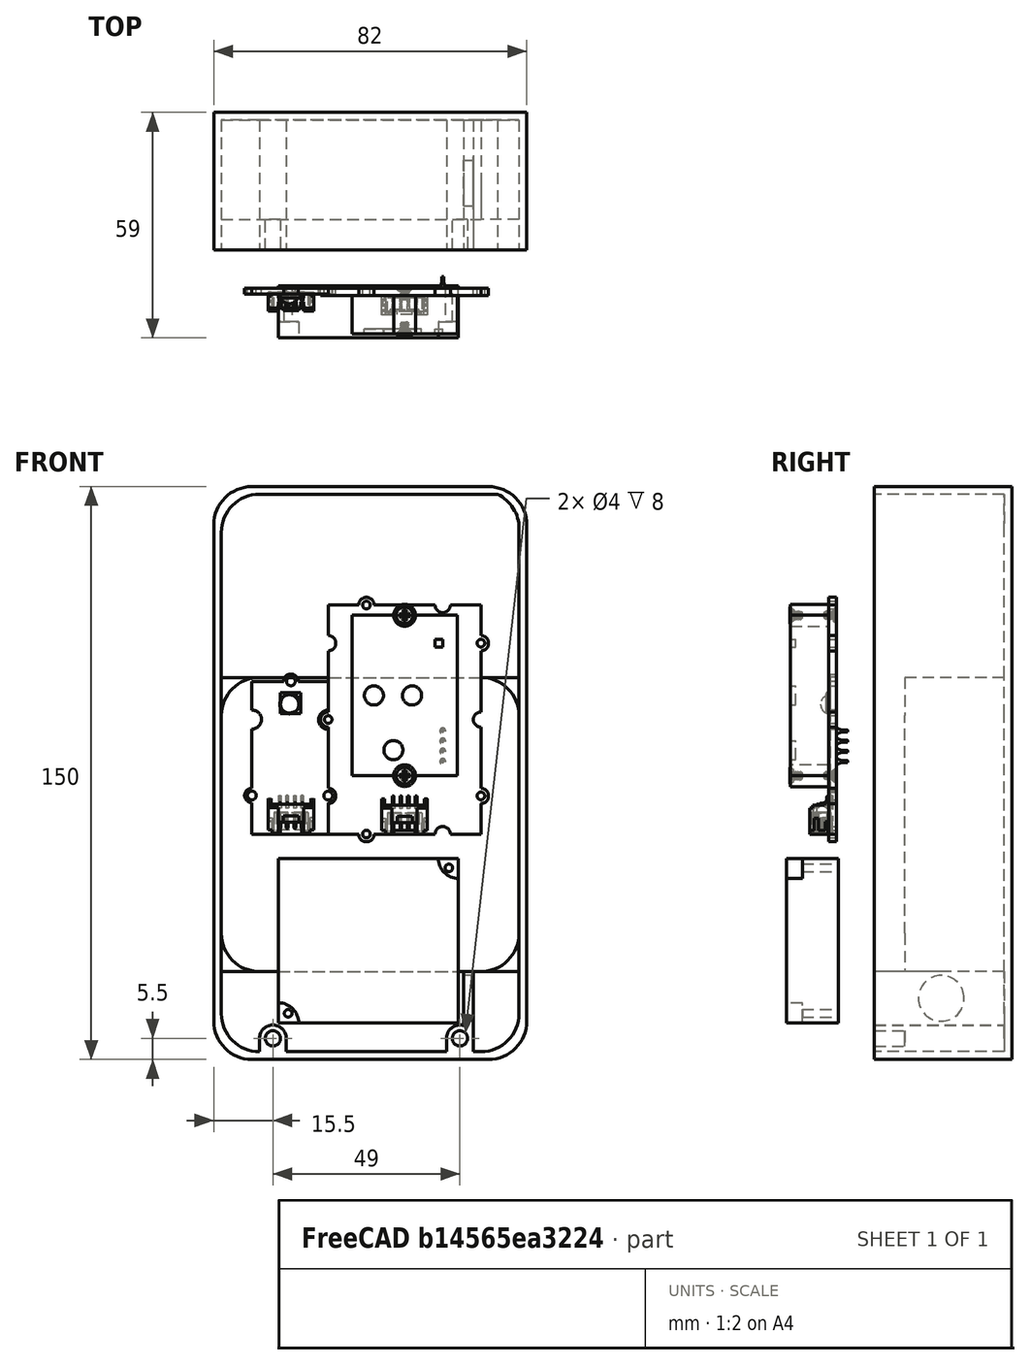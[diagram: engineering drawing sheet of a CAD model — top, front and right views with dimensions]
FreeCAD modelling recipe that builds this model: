
FCSTD DOCUMENT  (FreeCAD 0.20R29177 +233 (Git))
Label: wearableCad
License: All rights reserved
LicenseURL: http://en.wikipedia.org/wiki/All_rights_reserved
objects: Part::Cylinder×26, Part::Box×23, Part::Cut×22, Part::MultiFuse×11, Part::Feature×3
note: 85 computed .brp shape members not serialized (recipe doc carries the construction recipe); baked Part::Feature solids carry a one-line shape summary decoded from their .brp

FEATURE [Part::Feature] Feature  label="Odroid-C4"
  Placement = pos=(66,-10,0) rot=(0.57735,-0.57735,0.57735;2.0944rad)
  shape: bbox 57.1 x 20.65 x 89.5 mm, 2775 faces, 0 solids (baked)
FEATURE [Part::Feature] Feature001  label="SCD30"
  Placement = pos=(-1.3e-14,-22,57) rot=(0,-1,0;1.5708rad)
  shape: bbox 44 x 15.1 x 64 mm, 422 faces, 13 solids (baked)
FEATURE [Part::Feature] Feature002  label="bme280"
  Placement = pos=(-60,-20,58) rot=(0.707107,0,0.707107;3.14159rad)
  shape: bbox 23.8 x 6.016 x 41.9 mm, 221 faces, 2 solids (baked)
FEATURE [Part::MultiFuse] Fusion  label="i2cSensors"
  Placement = pos=(68,0,0) rot=(0,0,1;0rad)
  Shapes = -> [Feature001,Feature002]
FEATURE [Part::Box] Box  label="ips7100"
  AttacherType = Attacher::AttachEngine3D
  Height = 43.1
  Length = 47.1
  Width = 13.55
FEATURE [Part::Cylinder] Cylinder
  Angle = 360
  AttacherType = Attacher::AttachEngine3D
  FirstAngle = 0
  Height = 13.55
  Placement = pos=(2.5,13.55,2.5) rot=(1,0,0;1.5708rad)
  Radius = 1
  SecondAngle = 0
FEATURE [Part::Cylinder] Cylinder001  label="semiCut"
  Angle = 90
  AttacherType = Attacher::AttachEngine3D
  FirstAngle = 0
  Height = 4.13
  Placement = pos=(0,4.13,-9e-16) rot=(1,0,0;1.5708rad)
  Radius = 5.25
  SecondAngle = 0
FEATURE [Part::MultiFuse] Fusion001  label="ipsCut"
  Shapes = -> [Cylinder,Cylinder001]
FEATURE [Part::Cylinder] Cylinder002
  Angle = 360
  AttacherType = Attacher::AttachEngine3D
  FirstAngle = 0
  Height = 13.55
  Placement = pos=(2.5,13.55,2.5) rot=(1,0,0;1.5708rad)
  Radius = 1
  SecondAngle = 0
FEATURE [Part::Cylinder] Cylinder003  label="semiCut001"
  Angle = 90
  AttacherType = Attacher::AttachEngine3D
  FirstAngle = 0
  Height = 4.13
  Placement = pos=(0,4.13,-9e-16) rot=(1,0,0;1.5708rad)
  Radius = 5.25
  SecondAngle = 0
FEATURE [Part::MultiFuse] Fusion002  label="ipsCut001"
  Placement = pos=(47.1,0,43.1) rot=(0,1,0;3.14159rad)
  Shapes = -> [Cylinder002,Cylinder003]
FEATURE [Part::MultiFuse] Fusion003
  Shapes = -> [Fusion001,Fusion002]
FEATURE [Part::Cut] Cut  label="ips7100V"
  Base = -> Box
  Placement = pos=(15,-33,7.55) rot=(0,0,1;0rad)
  Tool = -> Fusion003
FEATURE [Part::Box] Box001  label="V25B"
  AttacherType = Attacher::AttachEngine3D
  Height = 77
  Length = 78
  Width = 26
FEATURE [Part::Cylinder] Cylinder004
  Angle = 90
  AttacherType = Attacher::AttachEngine3D
  FirstAngle = 0
  Height = 26
  Placement = pos=(0,26,-5.8e-15) rot=(1,0,0;1.5708rad)
  Radius = 10
  SecondAngle = 0
FEATURE [Part::Box] Box002  label="Cube"
  AttacherType = Attacher::AttachEngine3D
  Height = 10
  Length = 10
  Width = 26
FEATURE [Part::Cut] Cut001
  Base = -> Box002
  Placement = pos=(68,0,67) rot=(0,0,1;0rad)
  Tool = -> Cylinder004
FEATURE [Part::Box] Box003  label="Cube001"
  AttacherType = Attacher::AttachEngine3D
  Height = 10
  Length = 10
  Width = 26
FEATURE [Part::Cylinder] Cylinder005
  Angle = 90
  AttacherType = Attacher::AttachEngine3D
  FirstAngle = 0
  Height = 26
  Placement = pos=(0,26,-5.8e-15) rot=(1,0,0;1.5708rad)
  Radius = 10
  SecondAngle = 0
FEATURE [Part::Cut] Cut002
  Base = -> Box003
  Placement = pos=(68,0,10) rot=(0,1,0;1.5708rad)
  Tool = -> Cylinder005
FEATURE [Part::Box] Box004  label="Cube002"
  AttacherType = Attacher::AttachEngine3D
  Height = 10
  Length = 10
  Width = 26
FEATURE [Part::Cylinder] Cylinder006
  Angle = 90
  AttacherType = Attacher::AttachEngine3D
  FirstAngle = 0
  Height = 26
  Placement = pos=(0,26,-5.8e-15) rot=(1,0,0;1.5708rad)
  Radius = 10
  SecondAngle = 0
FEATURE [Part::Cut] Cut003
  Base = -> Box004
  Placement = pos=(10,0,10) rot=(0,1,0;3.14159rad)
  Tool = -> Cylinder006
FEATURE [Part::Box] Box005  label="Cube003"
  AttacherType = Attacher::AttachEngine3D
  Height = 10
  Length = 10
  Width = 26
FEATURE [Part::Cylinder] Cylinder007
  Angle = 90
  AttacherType = Attacher::AttachEngine3D
  FirstAngle = 0
  Height = 26
  Placement = pos=(0,26,-5.8e-15) rot=(1,0,0;1.5708rad)
  Radius = 10
  SecondAngle = 0
FEATURE [Part::Cut] Cut004
  Base = -> Box005
  Placement = pos=(10,0,67) rot=(0,-1,0;1.5708rad)
  Tool = -> Cylinder007
FEATURE [Part::MultiFuse] Fusion004  label="v25Cuts"
  Shapes = -> [Cut001,Cut002,Cut003,Cut004]
FEATURE [Part::Cut] Cut005  label="V25B001"
  Base = -> Box001
  Placement = pos=(0,-2,21) rot=(0,0,1;0rad)
  Tool = -> Fusion004
FEATURE [Part::Box] Box007  label="Cube004"
  AttacherType = Attacher::AttachEngine3D
  Height = 10
  Length = 10
  Placement = pos=(0,-10,0) rot=(0,0,1;0rad)
  Width = 36
FEATURE [Part::Cylinder] Cylinder008
  Angle = 90
  AttacherType = Attacher::AttachEngine3D
  FirstAngle = 0
  Height = 36
  Placement = pos=(0,26,-5.8e-15) rot=(1,0,0;1.5708rad)
  Radius = 10
  SecondAngle = 0
FEATURE [Part::Cut] Cut006
  Base = -> Box007
  Placement = pos=(8,18,8) rot=(-0.707107,0,0.707107;3.14159rad)
  Tool = -> Cylinder008
FEATURE [Part::Box] Box008  label="baseOut001"
  AttacherType = Attacher::AttachEngine3D
  Height = 150
  Length = 82
  Placement = pos=(80,26,-2) rot=(0,0,1;3.14159rad)
  Width = 36
FEATURE [Part::Box] Box009  label="Cube005"
  AttacherType = Attacher::AttachEngine3D
  Height = 10
  Length = 10
  Placement = pos=(0,-10,0) rot=(0,0,1;0rad)
  Width = 36
FEATURE [Part::Cylinder] Cylinder009
  Angle = 90
  AttacherType = Attacher::AttachEngine3D
  FirstAngle = 0
  Height = 36
  Placement = pos=(0,26,-5.8e-15) rot=(1,0,0;1.5708rad)
  Radius = 10
  SecondAngle = 0
FEATURE [Part::Cut] Cut007
  Base = -> Box009
  Placement = pos=(70,18,8) rot=(1,0,0;3.14159rad)
  Tool = -> Cylinder009
FEATURE [Part::Box] Box010  label="Cube006"
  AttacherType = Attacher::AttachEngine3D
  Height = 10
  Length = 10
  Placement = pos=(0,-10,0) rot=(0,0,1;0rad)
  Width = 36
FEATURE [Part::Cylinder] Cylinder010
  Angle = 90
  AttacherType = Attacher::AttachEngine3D
  FirstAngle = 0
  Height = 36
  Placement = pos=(0,26,-5.8e-15) rot=(1,0,0;1.5708rad)
  Radius = 10
  SecondAngle = 0
FEATURE [Part::Cut] Cut008
  Base = -> Box010
  Placement = pos=(8,18,138) rot=(0,0,1;3.14159rad)
  Tool = -> Cylinder010
FEATURE [Part::Box] Box011  label="Cube007"
  AttacherType = Attacher::AttachEngine3D
  Height = 10
  Length = 10
  Placement = pos=(0,-10,0) rot=(0,0,1;0rad)
  Width = 36
FEATURE [Part::Cylinder] Cylinder011
  Angle = 90
  AttacherType = Attacher::AttachEngine3D
  FirstAngle = 0
  Height = 36
  Placement = pos=(0,26,-5.8e-15) rot=(1,0,0;1.5708rad)
  Radius = 10
  SecondAngle = 0
FEATURE [Part::Cut] Cut009
  Base = -> Box011
  Placement = pos=(70,18,138) rot=(0.707107,0,0.707107;3.14159rad)
  Tool = -> Cylinder011
FEATURE [Part::MultiFuse] Fusion005
  Placement = pos=(0,-2,0) rot=(0,0,1;0rad)
  Shapes = -> [Cut006,Cut007,Cut008,Cut009]
FEATURE [Part::Cut] Cut010  label="BaseOut"
  Base = -> Box008
  Tool = -> Fusion005
FEATURE [Part::Box] Box013  label="Cube009"
  AttacherType = Attacher::AttachEngine3D
  Height = 10
  Length = 10
  Placement = pos=(0,-8,0) rot=(0,0,1;0rad)
  Width = 34
FEATURE [Part::Box] Box014  label="baseOut002"
  AttacherType = Attacher::AttachEngine3D
  Height = 146
  Length = 78
  Placement = pos=(80,26,-2) rot=(0,0,1;3.14159rad)
  Width = 34
FEATURE [Part::Box] Box015  label="Cube010"
  AttacherType = Attacher::AttachEngine3D
  Height = 10
  Length = 10
  Placement = pos=(0,-8,0) rot=(0,0,1;0rad)
  Width = 34
FEATURE [Part::Box] Box016  label="Cube011"
  AttacherType = Attacher::AttachEngine3D
  Height = 10
  Length = 10
  Placement = pos=(0,-8,0) rot=(0,0,1;0rad)
  Width = 34
FEATURE [Part::Box] Box017  label="Cube012"
  AttacherType = Attacher::AttachEngine3D
  Height = 10
  Length = 10
  Placement = pos=(0,-8,0) rot=(0,0,1;0rad)
  Width = 34
FEATURE [Part::Cylinder] Cylinder013
  Angle = 90
  AttacherType = Attacher::AttachEngine3D
  FirstAngle = 0
  Height = 34
  Placement = pos=(0,26,-5.8e-15) rot=(1,0,0;1.5708rad)
  Radius = 10
  SecondAngle = 0
FEATURE [Part::Cut] Cut012
  Base = -> Box013
  Placement = pos=(12,18,8) rot=(0.707107,0,-0.707107;3.14159rad)
  Tool = -> Cylinder013
FEATURE [Part::Cylinder] Cylinder014
  Angle = 90
  AttacherType = Attacher::AttachEngine3D
  FirstAngle = 0
  Height = 34
  Placement = pos=(0,26,-5.8e-15) rot=(1,0,0;1.5708rad)
  Radius = 10
  SecondAngle = 0
FEATURE [Part::Cut] Cut013
  Base = -> Box015
  Placement = pos=(70,18,8) rot=(1,0,0;3.14159rad)
  Tool = -> Cylinder014
FEATURE [Part::Cylinder] Cylinder015
  Angle = 90
  AttacherType = Attacher::AttachEngine3D
  FirstAngle = 0
  Height = 34
  Placement = pos=(0,26,-5.8e-15) rot=(1,0,0;1.5708rad)
  Radius = 10
  SecondAngle = 0
FEATURE [Part::Cut] Cut014
  Base = -> Box016
  Placement = pos=(12,18,134) rot=(0,0,1;3.14159rad)
  Tool = -> Cylinder015
FEATURE [Part::Cylinder] Cylinder016
  Angle = 90
  AttacherType = Attacher::AttachEngine3D
  FirstAngle = 0
  Height = 34
  Placement = pos=(0,26,-5.8e-15) rot=(1,0,0;1.5708rad)
  Radius = 10
  SecondAngle = 0
FEATURE [Part::Cut] Cut015
  Base = -> Box017
  Placement = pos=(70,18,135) rot=(0.707107,0,0.707107;3.14159rad)
  Tool = -> Cylinder016
FEATURE [Part::MultiFuse] Fusion006
  Shapes = -> [Cut012,Cut013,Cut014,Cut015]
FEATURE [Part::Cut] Cut016  label="BaseOut001"
  Base = -> Box014
  Placement = pos=(-2,-2,2) rot=(0,0,1;0rad)
  Tool = -> Fusion006
FEATURE [Part::Cut] Cut017  label="baseOut"
  Base = -> Cut010
  Tool = -> Cut016
FEATURE [Part::Box] Box018  label="Cube013"
  AttacherType = Attacher::AttachEngine3D
  Height = 10
  Length = 10
  Placement = pos=(10,26,0) rot=(0,0,-1;3.14159rad)
  Width = 26
FEATURE [Part::Cylinder] Cylinder017
  Angle = 90
  AttacherType = Attacher::AttachEngine3D
  FirstAngle = 0
  Height = 26
  Placement = pos=(0,26,-5.8e-15) rot=(1,0,0;1.5708rad)
  Radius = 10
  SecondAngle = 0
FEATURE [Part::Cut] Cut018  label="batterySupport"
  Base = -> Box018
  Placement = pos=(10,-2,31) rot=(0,1,0;3.14159rad)
  Tool = -> Cylinder017
FEATURE [Part::Box] Box019  label="Cube014"
  AttacherType = Attacher::AttachEngine3D
  Height = 10
  Length = 10
  Placement = pos=(10,26,0) rot=(0,0,1;3.14159rad)
  Width = 26
FEATURE [Part::Cylinder] Cylinder018
  Angle = 90
  AttacherType = Attacher::AttachEngine3D
  FirstAngle = 0
  Height = 26
  Placement = pos=(0,26,-5.8e-15) rot=(1,0,0;1.5708rad)
  Radius = 10
  SecondAngle = 0
FEATURE [Part::Cut] Cut019  label="batterySupport001"
  Base = -> Box019
  Placement = pos=(68,-2,31) rot=(0,-1,0;4.71239rad)
  Tool = -> Cylinder018
FEATURE [Part::Box] Box020  label="Cube015"
  AttacherType = Attacher::AttachEngine3D
  Height = 10
  Length = 10
  Placement = pos=(10,26,0) rot=(0,0,1;3.14159rad)
  Width = 26
FEATURE [Part::Cylinder] Cylinder019
  Angle = 90
  AttacherType = Attacher::AttachEngine3D
  FirstAngle = 0
  Height = 26
  Placement = pos=(0,26,-5.8e-15) rot=(1,0,0;1.5708rad)
  Radius = 10
  SecondAngle = 0
FEATURE [Part::Cut] Cut020  label="batterySupport002"
  Base = -> Box020
  Placement = pos=(68,-2,88) rot=(0,0,1;0rad)
  Tool = -> Cylinder019
FEATURE [Part::Box] Box021  label="Cube016"
  AttacherType = Attacher::AttachEngine3D
  Height = 10
  Length = 10
  Placement = pos=(10,26,0) rot=(0,0,1;3.14159rad)
  Width = 26
FEATURE [Part::Cylinder] Cylinder020
  Angle = 90
  AttacherType = Attacher::AttachEngine3D
  FirstAngle = 0
  Height = 26
  Placement = pos=(0,26,-5.8e-15) rot=(1,0,0;1.5708rad)
  Radius = 10
  SecondAngle = 0
FEATURE [Part::Cut] Cut021  label="batterySupport003"
  Base = -> Box021
  Placement = pos=(10,-2,88) rot=(0,1,0;4.71239rad)
  Tool = -> Cylinder020
FEATURE [Part::Cylinder] Cylinder021
  Angle = 360
  AttacherType = Attacher::AttachEngine3D
  FirstAngle = 0
  Height = 34
  Placement = pos=(13.5,24,3.5) rot=(1,0,0;1.5708rad)
  Radius = 3.5
  SecondAngle = 0
FEATURE [Part::Cylinder] Cylinder022
  Angle = 360
  AttacherType = Attacher::AttachEngine3D
  FirstAngle = 0
  Height = 8
  Placement = pos=(13.5,-2,3.5) rot=(1,0,0;1.5708rad)
  Radius = 2
  SecondAngle = 0
FEATURE [Part::Box] Box022  label="Cube017"
  AttacherType = Attacher::AttachEngine3D
  Height = 3.5
  Length = 7
  Placement = pos=(10,24,3.5) rot=(1,0,0;3.14159rad)
  Width = 34
FEATURE [Part::Cylinder] Cylinder023
  Angle = 360
  AttacherType = Attacher::AttachEngine3D
  FirstAngle = 0
  Height = 34
  Placement = pos=(62.5,24,3.5) rot=(1,0,0;1.5708rad)
  Radius = 3.5
  SecondAngle = 0
FEATURE [Part::Cylinder] Cylinder024
  Angle = 360
  AttacherType = Attacher::AttachEngine3D
  FirstAngle = 0
  Height = 8
  Placement = pos=(62.5,-2,3.5) rot=(1,0,0;1.5708rad)
  Radius = 2
  SecondAngle = 0
FEATURE [Part::Box] Box023  label="Cube018"
  AttacherType = Attacher::AttachEngine3D
  Height = 3.5
  Length = 7
  Placement = pos=(59,24,3.5) rot=(1,0,0;3.14159rad)
  Width = 34
FEATURE [Part::Cylinder] Cylinder025
  Angle = 360
  AttacherType = Attacher::AttachEngine3D
  FirstAngle = 0
  Height = 20
  Radius = 6
  SecondAngle = 0
FEATURE [Part::Cylinder] Cylinder026
  Angle = 360
  AttacherType = Attacher::AttachEngine3D
  FirstAngle = 0
  Height = 5
  Radius = 7
  SecondAngle = 0
FEATURE [Part::MultiFuse] Fusion007  label="powerSwitch"
  Placement = pos=(71,7.5,14) rot=(0,1,0;4.71239rad)
  Shapes = -> [Cylinder025,Cylinder026]
FEATURE [Part::Box] Box024  label="Cube019"
  AttacherType = Attacher::AttachEngine3D
  Height = 17.5
  Length = 2.5
  Placement = pos=(63.5,24,21) rot=(1,0,0;3.14159rad)
  Width = 34
FEATURE [Part::MultiFuse] Fusion008  label="base"
  Shapes = -> [Cut017,Cut018,Cut019,Cut020,Cut021]
FEATURE [Part::MultiFuse] Fusion009  label="base001"
  Shapes = -> [Cylinder021,Cylinder023,Box022,Box023,Box024,Fusion008]
FEATURE [Part::MultiFuse] Fusion010  label="baseCuts"
  Shapes = -> [Cylinder024,Cylinder022,Fusion007]
FEATURE [Part::Cut] Cut022  label="baseCuts001"
  Base = -> Fusion009
  Tool = -> Fusion010
